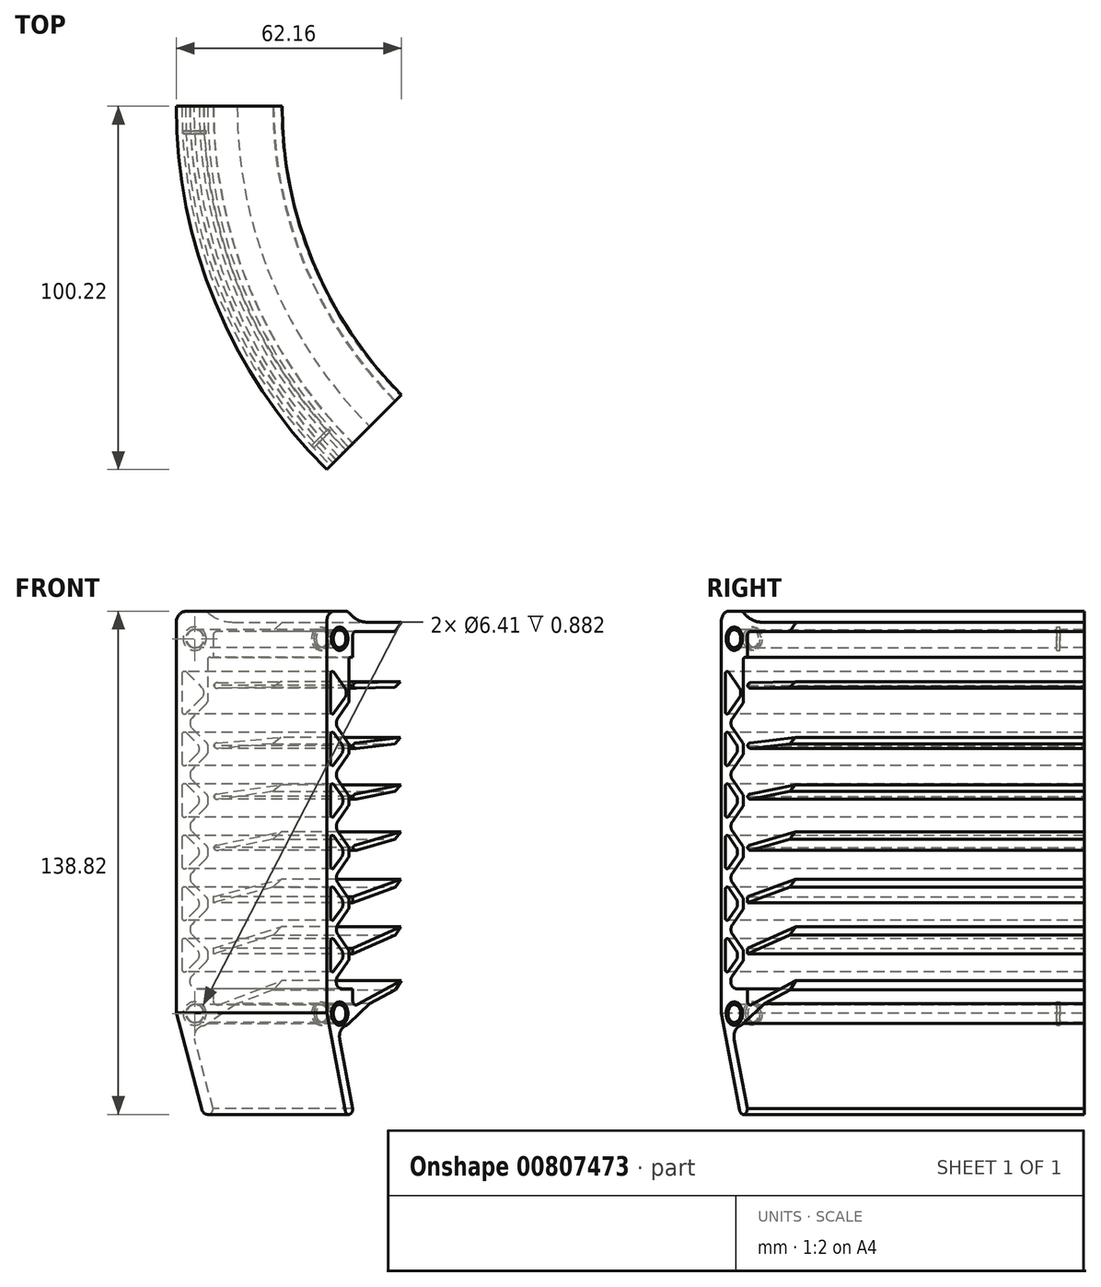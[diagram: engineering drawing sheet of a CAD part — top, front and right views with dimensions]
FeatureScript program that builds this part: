
annotation { "Feature Type Name" : "Feature", "Feature Type Description" : "" }
export const myFeature = defineFeature(function(context is Context, id is Id, definition is map)
    precondition{}
    {
        {
            var Q0;
            Q0=qCreatedBy(makeId("Front.planeOp"),FACE);
            var sketch = newSketch(context, id + "F0", { "sketchPlane" : qUnion([Q0])});
            skLineSegment(sketch, "E0", {"start": v(0, 0) * mm, "end": v(-133.7, 0) * mm, "construction": true});
            skLineSegment(sketch, "E1", {"start": v(-141.73, 0) * mm, "end": v(-141.73, 111.25) * mm});
            skLineSegment(sketch, "E2", {"start": v(-138.68, 114.3) * mm, "end": v(-134.62, 114.3) * mm});
            skLineSegment(sketch, "E3", {"start": v(-131.57, 111.25) * mm, "end": v(-131.57, 0) * mm});
            skLineSegment(sketch, "E4", {"start": v(-135.3, 101.6) * mm, "end": v(-131.57, 101.6) * mm});
            skLineSegment(sketch, "E5", {"start": v(-135.99, 10.16) * mm, "end": v(-131.57, 10.16) * mm});
            skLineSegment(sketch, "E6", {"start": v(-141.73, 3.56) * mm, "end": v(-134.54, -23.4) * mm});
            skLineSegment(sketch, "E7", {"start": v(-131.57, -23) * mm, "end": v(-131.57, -22.86) * mm});
            skLineSegment(sketch, "E8", {"start": v(-131.57, -22.86) * mm, "end": v(-136.65, -3.83) * mm});
            skPoint(sketch, "E9.visualSharp", {"position": v(-131.57, -34.54) * mm});
            skArc(sketch, "E9.filletArc", {"start": v(-134.54, -23.4) * mm, "mid": v(-132.89, -24.5) * mm, "end": v(-131.57, -23) * mm});
            skPoint(sketch, "E10.newPointA", {"position": v(-136.65, -3.8) * mm});
            skPoint(sketch, "E10.newPointB", {"position": v(-141.73, 0) * mm});
            skArc(sketch, "E10.filletArc", {"start": v(-133.7, 0) * mm, "mid": v(-136.12, -1.2) * mm, "end": v(-136.65, -3.83) * mm});
            skPoint(sketch, "E11.visualSharp", {"position": v(-141.73, 114.3) * mm});
            skArc(sketch, "E11.filletArc", {"start": v(-138.68, 114.3) * mm, "mid": v(-140.84, 113.4) * mm, "end": v(-141.73, 111.25) * mm});
            skPoint(sketch, "E12.visualSharp", {"position": v(-131.57, 114.3) * mm});
            skArc(sketch, "E12.filletArc", {"start": v(-131.57, 111.25) * mm, "mid": v(-132.46, 113.4) * mm, "end": v(-134.62, 114.3) * mm});
            skLineSegment(sketch, "E13.bottom", {"start": v(-140.2, 101.6) * mm, "end": v(-133.1, 101.6) * mm});
            skLineSegment(sketch, "E13.top", {"start": v(-140.2, 10.16) * mm, "end": v(-133.1, 10.16) * mm});
            skLineSegment(sketch, "E13.left", {"start": v(-140.2, 101.6) * mm, "end": v(-140.2, 10.16) * mm});
            skLineSegment(sketch, "E13.right", {"start": v(-133.1, 101.6) * mm, "end": v(-133.1, 10.16) * mm});
            skLineSegment(sketch, "E14", {"start": v(-136.74, 98.13) * mm, "end": v(-133.1, 94.49) * mm});
            skLineSegment(sketch, "E15", {"start": v(-134.7, 90.35) * mm, "end": v(-140.2, 84.84) * mm});
            skLineSegment(sketch, "E16", {"start": v(-137.34, 81.96) * mm, "end": v(-133.1, 77.72) * mm});
            skLineSegment(sketch, "E17", {"start": v(-135.97, 74.85) * mm, "end": v(-140.2, 70.61) * mm});
            skLineSegment(sketch, "E18", {"start": v(-137.34, 67.74) * mm, "end": v(-133.1, 63.5) * mm});
            skLineSegment(sketch, "E19", {"start": v(-135.97, 60.63) * mm, "end": v(-140.2, 56.39) * mm});
            skLineSegment(sketch, "E20", {"start": v(-137.34, 53.52) * mm, "end": v(-133.1, 49.28) * mm});
            skLineSegment(sketch, "E21", {"start": v(-135.97, 46.4) * mm, "end": v(-140.2, 42.16) * mm});
            skLineSegment(sketch, "E22", {"start": v(-137.34, 39.3) * mm, "end": v(-133.1, 35.05) * mm});
            skLineSegment(sketch, "E23", {"start": v(-135.97, 32.18) * mm, "end": v(-140.2, 27.94) * mm});
            skLineSegment(sketch, "E24", {"start": v(-137.34, 25.07) * mm, "end": v(-133.1, 20.83) * mm});
            skLineSegment(sketch, "E25", {"start": v(-135.97, 17.96) * mm, "end": v(-140.2, 13.72) * mm});
            skLineSegment(sketch, "E26.1.0.0", {"start": v(-133.1, 32.18) * mm, "end": v(-137.34, 27.94) * mm});
            skLineSegment(sketch, "E26.1.0.1", {"start": v(-140.2, 39.3) * mm, "end": v(-135.97, 35.05) * mm});
            skLineSegment(sketch, "E26.1.0.2", {"start": v(-140.2, 25.07) * mm, "end": v(-135.97, 20.83) * mm});
            skLineSegment(sketch, "E26.1.0.3", {"start": v(-133.1, 17.96) * mm, "end": v(-137.42, 13.63) * mm});
            skLineSegment(sketch, "E26.1.0.4", {"start": v(-133.1, 46.4) * mm, "end": v(-137.34, 42.17) * mm});
            skLineSegment(sketch, "E26.1.0.5", {"start": v(-140.2, 53.52) * mm, "end": v(-135.97, 49.28) * mm});
            skLineSegment(sketch, "E26.1.0.6", {"start": v(-133.1, 60.63) * mm, "end": v(-137.34, 56.39) * mm});
            skLineSegment(sketch, "E26.1.0.7", {"start": v(-140.2, 67.74) * mm, "end": v(-135.97, 63.5) * mm});
            skLineSegment(sketch, "E26.1.0.8", {"start": v(-133.1, 74.85) * mm, "end": v(-137.34, 70.61) * mm});
            skLineSegment(sketch, "E26.1.0.9", {"start": v(-140.2, 81.97) * mm, "end": v(-135.97, 77.73) * mm});
            skLineSegment(sketch, "E26.1.0.10", {"start": v(-133.1, 89.08) * mm, "end": v(-137.34, 84.84) * mm});
            skLineSegment(sketch, "E26.1.0.11", {"start": v(-140.2, 98.73) * mm, "end": v(-134.7, 93.22) * mm});
            skLineSegment(sketch, "E26.direction1", {"start": v(-140.2, 13.72) * mm, "end": v(-140.2, 11.43) * mm, "construction": true});
            skPoint(sketch, "E27.newPointA", {"position": v(-140.2, 101.6) * mm});
            skArc(sketch, "E27.filletArc", {"start": v(-135.3, 101.6) * mm, "mid": v(-137.18, 100.35) * mm, "end": v(-136.74, 98.13) * mm});
            skPoint(sketch, "E28.newPointA", {"position": v(-140.2, 10.85) * mm});
            skArc(sketch, "E28.filletArc", {"start": v(-137.42, 13.63) * mm, "mid": v(-137.87, 11.41) * mm, "end": v(-135.99, 10.16) * mm});
            skPoint(sketch, "E29.newPointA", {"position": v(-133.1, 17.96) * mm});
            skPoint(sketch, "E29.newPointB", {"position": v(-133.1, 20.83) * mm});
            skArc(sketch, "E29.filletArc", {"start": v(-135.97, 17.96) * mm, "mid": v(-135.37, 19.4) * mm, "end": v(-135.97, 20.83) * mm});
            skPoint(sketch, "E30.newPointA", {"position": v(-140.2, 27.94) * mm});
            skPoint(sketch, "E30.newPointB", {"position": v(-140.2, 25.07) * mm});
            skArc(sketch, "E30.filletArc", {"start": v(-137.34, 27.94) * mm, "mid": v(-137.93, 26.5) * mm, "end": v(-137.34, 25.07) * mm});
            skPoint(sketch, "E31.newPointA", {"position": v(-140.2, 42.16) * mm});
            skPoint(sketch, "E31.newPointB", {"position": v(-140.2, 39.3) * mm});
            skArc(sketch, "E31.filletArc", {"start": v(-137.34, 42.17) * mm, "mid": v(-137.93, 40.73) * mm, "end": v(-137.34, 39.3) * mm});
            skPoint(sketch, "E32.newPointA", {"position": v(-133.1, 49.28) * mm});
            skPoint(sketch, "E32.newPointB", {"position": v(-133.1, 46.4) * mm});
            skArc(sketch, "E32.filletArc", {"start": v(-135.97, 46.4) * mm, "mid": v(-135.37, 47.84) * mm, "end": v(-135.97, 49.28) * mm});
            skPoint(sketch, "E33.newPointA", {"position": v(-140.2, 56.39) * mm});
            skPoint(sketch, "E33.newPointB", {"position": v(-140.2, 53.52) * mm});
            skArc(sketch, "E33.filletArc", {"start": v(-137.34, 56.39) * mm, "mid": v(-137.93, 54.95) * mm, "end": v(-137.34, 53.52) * mm});
            skPoint(sketch, "E34.newPointA", {"position": v(-133.1, 63.5) * mm});
            skPoint(sketch, "E34.newPointB", {"position": v(-133.1, 60.63) * mm});
            skArc(sketch, "E34.filletArc", {"start": v(-135.97, 60.63) * mm, "mid": v(-135.37, 62.06) * mm, "end": v(-135.97, 63.5) * mm});
            skPoint(sketch, "E35.newPointA", {"position": v(-140.2, 70.61) * mm});
            skPoint(sketch, "E35.newPointB", {"position": v(-140.2, 67.74) * mm});
            skArc(sketch, "E35.filletArc", {"start": v(-137.34, 70.61) * mm, "mid": v(-137.93, 69.18) * mm, "end": v(-137.34, 67.74) * mm});
            skPoint(sketch, "E36.newPointA", {"position": v(-133.1, 35.05) * mm});
            skPoint(sketch, "E36.newPointB", {"position": v(-133.1, 32.18) * mm});
            skArc(sketch, "E36.filletArc", {"start": v(-135.97, 32.18) * mm, "mid": v(-135.37, 33.62) * mm, "end": v(-135.97, 35.05) * mm});
            skPoint(sketch, "E37.newPointA", {"position": v(-133.1, 77.72) * mm});
            skPoint(sketch, "E37.newPointB", {"position": v(-133.1, 74.85) * mm});
            skArc(sketch, "E37.filletArc", {"start": v(-135.97, 74.85) * mm, "mid": v(-135.37, 76.29) * mm, "end": v(-135.97, 77.73) * mm});
            skPoint(sketch, "E38.newPointA", {"position": v(-140.2, 84.84) * mm});
            skPoint(sketch, "E38.newPointB", {"position": v(-140.2, 81.97) * mm});
            skArc(sketch, "E38.filletArc", {"start": v(-137.34, 84.84) * mm, "mid": v(-137.93, 83.4) * mm, "end": v(-137.34, 81.96) * mm});
            skPoint(sketch, "E39.newPointA", {"position": v(-133.1, 91.95) * mm});
            skPoint(sketch, "E39.newPointB", {"position": v(-133.1, 91.62) * mm});
            skArc(sketch, "E39.filletArc", {"start": v(-134.7, 90.35) * mm, "mid": v(-134.1, 91.78) * mm, "end": v(-134.7, 93.22) * mm});
            skLineSegment(sketch, "E40", {"start": v(-136.65, -3.56) * mm, "end": v(-136.65, 10.16) * mm, "construction": true});
            skLineSegment(sketch, "E41", {"start": v(-136.65, 101.6) * mm, "end": v(-136.65, 106.68) * mm, "construction": true});
            skCircle(sketch, "E42", {"center": v(-136.65, 106.68) * mm, "radius": 2.48 * mm});
            skCircle(sketch, "E43", {"center": v(-136.65, 3.3) * mm, "radius": 2.48 * mm});
            skPoint(sketch, "E43.perimeterSnap0", {"position": v(-136.65, 3.3) * mm});
            skPoint(sketch, "E43.perimeterSnap1", {"position": v(-133.78, 10.16) * mm});
            skLineSegment(sketch, "E44", {"start": v(0, 0) * mm, "end": v(0, 14.7) * mm, "construction": true});
            skLineSegment(sketch, "E45", {"start": v(-111.76, 0) * mm, "end": v(-111.76, 130.03) * mm, "construction": true});
            skLineSegment(sketch, "E46", {"start": v(-131.57, 111.25) * mm, "end": v(-111.76, 111.25) * mm});
            skLineSegment(sketch, "E47", {"start": v(-111.76, 111.25) * mm, "end": v(-111.76, 108.71) * mm});
            skLineSegment(sketch, "E48", {"start": v(-111.76, 108.71) * mm, "end": v(-131.57, 108.71) * mm});
            skLineSegment(sketch, "E49", {"start": v(-111.76, 111.25) * mm, "end": v(111.76, 111.25) * mm, "construction": true});
            skLineSegment(sketch, "E50", {"start": v(111.76, 111.25) * mm, "end": v(111.76, 98.55) * mm, "construction": true});
            skLineSegment(sketch, "E51", {"start": v(-133.1, 94.49) * mm, "end": v(111.76, 98.55) * mm, "construction": true});
            skLineSegment(sketch, "E52", {"start": v(111.76, 98.55) * mm, "end": v(-133.1, 77.72) * mm, "construction": true});
            skLineSegment(sketch, "E53", {"start": v(111.76, 98.55) * mm, "end": v(-133.1, 63.5) * mm, "construction": true});
            skLineSegment(sketch, "E54", {"start": v(-133.1, 49.28) * mm, "end": v(111.76, 98.55) * mm, "construction": true});
            skLineSegment(sketch, "E55", {"start": v(-133.1, 35.05) * mm, "end": v(111.76, 98.55) * mm, "construction": true});
            skLineSegment(sketch, "E56", {"start": v(-133.1, 20.83) * mm, "end": v(111.76, 98.55) * mm, "construction": true});
            skLineSegment(sketch, "E57", {"start": v(-131.57, 10.16) * mm, "end": v(-131.57, 0) * mm, "construction": true});
            skLineSegment(sketch, "E58", {"start": v(-131.57, 5.08) * mm, "end": v(111.76, 98.55) * mm, "construction": true});
            skLineSegment(sketch, "E59", {"start": v(-131.57, 94.51) * mm, "end": v(-111.76, 94.84) * mm});
            skLineSegment(sketch, "E60", {"start": v(-111.76, 94.84) * mm, "end": v(-111.76, 93.32) * mm});
            skLineSegment(sketch, "E61", {"start": v(-111.76, 93.32) * mm, "end": v(-131.57, 92.99) * mm});
            skLineSegment(sketch, "E62", {"start": v(-131.57, 77.85) * mm, "end": v(-111.76, 79.54) * mm});
            skLineSegment(sketch, "E63", {"start": v(-111.76, 79.54) * mm, "end": v(-111.76, 78) * mm});
            skLineSegment(sketch, "E64", {"start": v(-111.76, 78) * mm, "end": v(-131.57, 76.32) * mm});
            skLineSegment(sketch, "E65", {"start": v(-131.57, 63.72) * mm, "end": v(-111.76, 66.55) * mm});
            skLineSegment(sketch, "E66", {"start": v(-111.76, 66.55) * mm, "end": v(-111.76, 65.01) * mm});
            skLineSegment(sketch, "E67", {"start": v(-111.76, 65.01) * mm, "end": v(-131.57, 62.18) * mm});
            skLineSegment(sketch, "E68", {"start": v(-131.57, 49.58) * mm, "end": v(-111.76, 53.57) * mm});
            skLineSegment(sketch, "E69", {"start": v(-111.76, 53.57) * mm, "end": v(-111.76, 52.02) * mm});
            skLineSegment(sketch, "E70", {"start": v(-111.76, 52.02) * mm, "end": v(-131.57, 48.03) * mm});
            skLineSegment(sketch, "E71", {"start": v(-131.57, 35.45) * mm, "end": v(-111.76, 40.59) * mm});
            skLineSegment(sketch, "E72", {"start": v(-111.76, 40.59) * mm, "end": v(-111.76, 39.01) * mm});
            skLineSegment(sketch, "E73", {"start": v(-111.76, 39.01) * mm, "end": v(-131.57, 33.87) * mm});
            skLineSegment(sketch, "E74", {"start": v(-131.57, 21.31) * mm, "end": v(-111.76, 27.6) * mm});
            skLineSegment(sketch, "E75", {"start": v(-111.76, 27.6) * mm, "end": v(-111.76, 26) * mm});
            skLineSegment(sketch, "E76", {"start": v(-111.76, 26) * mm, "end": v(-131.57, 19.71) * mm});
            skLineSegment(sketch, "E77", {"start": v(-131.57, 5.08) * mm, "end": v(-111.76, 12.7) * mm});
            skLineSegment(sketch, "E78", {"start": v(-111.76, 12.7) * mm, "end": v(-111.76, 11.06) * mm});
            skLineSegment(sketch, "E79", {"start": v(-111.76, 11.06) * mm, "end": v(-131.57, 3.45) * mm});
            skLineSegment(sketch, "E80", {"start": v(-133.7, 0) * mm, "end": v(-131.57, 0) * mm});
            skLineSegment(sketch, "E81", {"start": v(-111.76, 111.25) * mm, "end": v(-110.33, 111.25) * mm});
            skLineSegment(sketch, "E82", {"start": v(-110.33, 111.25) * mm, "end": v(-111.76, 108.71) * mm});
            skSolve(sketch);
        }
        {
            var Q0;
            {var subQ0=sQuery(id+"F0.wireOp",EDGE,"E6");Q0=makeQuery(id+"F0.imprint","IMPRINT",FACE,{"disambiguationData":[TD([[makeQuery(id+"F0.imprint","IMPRINT",EDGE,{"derivedFrom":subQ0}),1.0]])]});}
            var Q1;
            {var subQ22=sQuery(id+"F0.wireOp",EDGE,"E1");Q1=makeQuery(id+"F0.imprint","IMPRINT",FACE,{"disambiguationData":[TD([[makeQuery(id+"F0.imprint","IMPRINT",EDGE,{"derivedFrom":subQ22}),-1.0]])]});}
            var Q2;
            {var subQ8=sQuery(id+"F0.wireOp",EDGE,"E4");Q2=makeQuery(id+"F0.imprint","IMPRINT",FACE,{"disambiguationData":[TD([[makeQuery(id+"F0.imprint","IMPRINT",EDGE,{"derivedFrom":subQ8}),-1.0]])]});}
            var Q3;
            {var subQ14=sQuery(id+"F0.wireOp",EDGE,"E14");Q3=makeQuery(id+"F0.imprint","IMPRINT",FACE,{"disambiguationData":[TD([[makeQuery(id+"F0.imprint","IMPRINT",EDGE,{"derivedFrom":subQ14}),-1.0]])]});}
            var Q4;
            {var subQ0=sQuery(id+"F0.wireOp",EDGE,"E46");Q4=makeQuery(id+"F0.imprint","IMPRINT",FACE,{"disambiguationData":[TD([[makeQuery(id+"F0.imprint","IMPRINT",EDGE,{"derivedFrom":subQ0}),-1.0]])]});}
            var Q5;
            {var subQ0=sQuery(id+"F0.wireOp",EDGE,"E59");Q5=makeQuery(id+"F0.imprint","IMPRINT",FACE,{"disambiguationData":[TD([[makeQuery(id+"F0.imprint","IMPRINT",EDGE,{"derivedFrom":subQ0}),-1.0]])]});}
            var Q6;
            {var subQ0=sQuery(id+"F0.wireOp",EDGE,"E62");Q6=makeQuery(id+"F0.imprint","IMPRINT",FACE,{"disambiguationData":[TD([[makeQuery(id+"F0.imprint","IMPRINT",EDGE,{"derivedFrom":subQ0}),-1.0]])]});}
            var Q7;
            {var subQ0=sQuery(id+"F0.wireOp",EDGE,"E65");Q7=makeQuery(id+"F0.imprint","IMPRINT",FACE,{"disambiguationData":[TD([[makeQuery(id+"F0.imprint","IMPRINT",EDGE,{"derivedFrom":subQ0}),-1.0]])]});}
            var Q8;
            {var subQ0=sQuery(id+"F0.wireOp",EDGE,"E68");Q8=makeQuery(id+"F0.imprint","IMPRINT",FACE,{"disambiguationData":[TD([[makeQuery(id+"F0.imprint","IMPRINT",EDGE,{"derivedFrom":subQ0}),-1.0]])]});}
            var Q9;
            {var subQ0=sQuery(id+"F0.wireOp",EDGE,"E71");Q9=makeQuery(id+"F0.imprint","IMPRINT",FACE,{"disambiguationData":[TD([[makeQuery(id+"F0.imprint","IMPRINT",EDGE,{"derivedFrom":subQ0}),-1.0]])]});}
            var Q10;
            {var subQ0=sQuery(id+"F0.wireOp",EDGE,"E74");Q10=makeQuery(id+"F0.imprint","IMPRINT",FACE,{"disambiguationData":[TD([[makeQuery(id+"F0.imprint","IMPRINT",EDGE,{"derivedFrom":subQ0}),-1.0]])]});}
            var Q11;
            {var subQ0=sQuery(id+"F0.wireOp",EDGE,"E77");Q11=makeQuery(id+"F0.imprint","IMPRINT",FACE,{"disambiguationData":[TD([[makeQuery(id+"F0.imprint","IMPRINT",EDGE,{"derivedFrom":subQ0}),-1.0]])]});}
            var Q12;
            Q12=sQuery(id+"F0.wireOp",EDGE,"E44");
            revolve(context, id + "F1", {"surfaceOperationType" : NewSurfaceOperationType.NEW, "entities" : qUnion([Q0, Q1, Q2, Q3, Q4, Q5, Q6, Q7, Q8, Q9, Q10, Q11]), "axis" : qUnion([Q12]), "revolveType" : RevolveType.ONE_DIRECTION, "angle" : 45 * degree});
        }
        {
            var Q0;
            Q0=makeQuery(id+"F1.opRevolve","SWEPT_EDGE",EDGE,{"disambiguationData":[OSD([sQuery(id+"F0.wireOp",EDGE,"E47"),sQuery(id+"F0.wireOp",EDGE,"E48")])]});
            chamfer(context, id + "F2", {"entities" : qUnion([Q0]), "width" : 3.3 * mm, "tangentPropagation" : true});
        }
        {
            var Q0;
            Q0=makeQuery(id+"F1.opRevolve","SWEPT_EDGE",EDGE,{"disambiguationData":[OSD([sQuery(id+"F0.wireOp",EDGE,"E60"),sQuery(id+"F0.wireOp",EDGE,"E61")])]});
            var Q1;
            Q1=makeQuery(id+"F1.opRevolve","SWEPT_EDGE",EDGE,{"disambiguationData":[OSD([sQuery(id+"F0.wireOp",EDGE,"E63"),sQuery(id+"F0.wireOp",EDGE,"E64")])]});
            var Q2;
            Q2=makeQuery(id+"F1.opRevolve","SWEPT_EDGE",EDGE,{"disambiguationData":[OSD([sQuery(id+"F0.wireOp",EDGE,"E66"),sQuery(id+"F0.wireOp",EDGE,"E67")])]});
            var Q3;
            Q3=makeQuery(id+"F1.opRevolve","SWEPT_EDGE",EDGE,{"disambiguationData":[OSD([sQuery(id+"F0.wireOp",EDGE,"E69"),sQuery(id+"F0.wireOp",EDGE,"E70")])]});
            var Q4;
            Q4=makeQuery(id+"F1.opRevolve","SWEPT_EDGE",EDGE,{"disambiguationData":[OSD([sQuery(id+"F0.wireOp",EDGE,"E72"),sQuery(id+"F0.wireOp",EDGE,"E73")])]});
            var Q5;
            Q5=makeQuery(id+"F1.opRevolve","SWEPT_EDGE",EDGE,{"disambiguationData":[OSD([sQuery(id+"F0.wireOp",EDGE,"E75"),sQuery(id+"F0.wireOp",EDGE,"E76")])]});
            var Q6;
            Q6=makeQuery(id+"F1.opRevolve","SWEPT_EDGE",EDGE,{"disambiguationData":[OSD([sQuery(id+"F0.wireOp",EDGE,"E78"),sQuery(id+"F0.wireOp",EDGE,"E79")])]});
            chamfer(context, id + "F3", {"entities" : qUnion([Q0, Q1, Q2, Q3, Q4, Q5, Q6]), "chamferType" : ChamferType.TWO_OFFSETS, "width1" : 2.3 * mm, "oppositeDirection" : false, "width2" : 3.3 * mm, "tangentPropagation" : true});
        }
        {
            var Q0;
            Q0=makeQuery(id+"F1.opRevolve","CAP_FACE",FACE,{"disambiguationData":[OSD([sQuery(id+"F0.wireOp",EDGE,"E1"),sQuery(id+"F0.wireOp",EDGE,"E2"),sQuery(id+"F0.wireOp",EDGE,"E3"),sQuery(id+"F0.wireOp",EDGE,"E6"),sQuery(id+"F0.wireOp",EDGE,"E7"),sQuery(id+"F0.wireOp",EDGE,"E8"),sQuery(id+"F0.wireOp",EDGE,"E9.filletArc"),sQuery(id+"F0.wireOp",EDGE,"E10.filletArc"),sQuery(id+"F0.wireOp",EDGE,"E11.filletArc"),sQuery(id+"F0.wireOp",EDGE,"E12.filletArc"),sQuery(id+"F0.wireOp",EDGE,"E13.bottom"),sQuery(id+"F0.wireOp",EDGE,"E13.top"),sQuery(id+"F0.wireOp",EDGE,"E13.left"),sQuery(id+"F0.wireOp",EDGE,"E13.right"),sQuery(id+"F0.wireOp",EDGE,"E14"),sQuery(id+"F0.wireOp",EDGE,"E15"),sQuery(id+"F0.wireOp",EDGE,"E16"),sQuery(id+"F0.wireOp",EDGE,"E17"),sQuery(id+"F0.wireOp",EDGE,"E18"),sQuery(id+"F0.wireOp",EDGE,"E19"),sQuery(id+"F0.wireOp",EDGE,"E20"),sQuery(id+"F0.wireOp",EDGE,"E21"),sQuery(id+"F0.wireOp",EDGE,"E22"),sQuery(id+"F0.wireOp",EDGE,"E23"),sQuery(id+"F0.wireOp",EDGE,"E24"),sQuery(id+"F0.wireOp",EDGE,"E25"),sQuery(id+"F0.wireOp",EDGE,"E26.1.0.0"),sQuery(id+"F0.wireOp",EDGE,"E26.1.0.1"),sQuery(id+"F0.wireOp",EDGE,"E26.1.0.2"),sQuery(id+"F0.wireOp",EDGE,"E26.1.0.3"),sQuery(id+"F0.wireOp",EDGE,"E26.1.0.4"),sQuery(id+"F0.wireOp",EDGE,"E26.1.0.5"),sQuery(id+"F0.wireOp",EDGE,"E26.1.0.6"),sQuery(id+"F0.wireOp",EDGE,"E26.1.0.7"),sQuery(id+"F0.wireOp",EDGE,"E26.1.0.8"),sQuery(id+"F0.wireOp",EDGE,"E26.1.0.9"),sQuery(id+"F0.wireOp",EDGE,"E26.1.0.10"),sQuery(id+"F0.wireOp",EDGE,"E26.1.0.11"),sQuery(id+"F0.wireOp",EDGE,"E27.filletArc"),sQuery(id+"F0.wireOp",EDGE,"E28.filletArc"),sQuery(id+"F0.wireOp",EDGE,"E29.filletArc"),sQuery(id+"F0.wireOp",EDGE,"E30.filletArc"),sQuery(id+"F0.wireOp",EDGE,"E31.filletArc"),sQuery(id+"F0.wireOp",EDGE,"E32.filletArc"),sQuery(id+"F0.wireOp",EDGE,"E33.filletArc"),sQuery(id+"F0.wireOp",EDGE,"E34.filletArc"),sQuery(id+"F0.wireOp",EDGE,"E35.filletArc"),sQuery(id+"F0.wireOp",EDGE,"E36.filletArc"),sQuery(id+"F0.wireOp",EDGE,"E37.filletArc"),sQuery(id+"F0.wireOp",EDGE,"E38.filletArc"),sQuery(id+"F0.wireOp",EDGE,"E39.filletArc"),sQuery(id+"F0.wireOp",EDGE,"E42"),sQuery(id+"F0.wireOp",EDGE,"E43"),sQuery(id+"F0.wireOp",EDGE,"E46"),sQuery(id+"F0.wireOp",EDGE,"E47"),sQuery(id+"F0.wireOp",EDGE,"E48"),sQuery(id+"F0.wireOp",EDGE,"E59"),sQuery(id+"F0.wireOp",EDGE,"E60"),sQuery(id+"F0.wireOp",EDGE,"E61"),sQuery(id+"F0.wireOp",EDGE,"E62"),sQuery(id+"F0.wireOp",EDGE,"E63"),sQuery(id+"F0.wireOp",EDGE,"E64"),sQuery(id+"F0.wireOp",EDGE,"E65"),sQuery(id+"F0.wireOp",EDGE,"E66"),sQuery(id+"F0.wireOp",EDGE,"E67"),sQuery(id+"F0.wireOp",EDGE,"E68"),sQuery(id+"F0.wireOp",EDGE,"E69"),sQuery(id+"F0.wireOp",EDGE,"E70"),sQuery(id+"F0.wireOp",EDGE,"E71"),sQuery(id+"F0.wireOp",EDGE,"E72"),sQuery(id+"F0.wireOp",EDGE,"E73"),sQuery(id+"F0.wireOp",EDGE,"E74"),sQuery(id+"F0.wireOp",EDGE,"E75"),sQuery(id+"F0.wireOp",EDGE,"E76"),sQuery(id+"F0.wireOp",EDGE,"E77"),sQuery(id+"F0.wireOp",EDGE,"E78"),sQuery(id+"F0.wireOp",EDGE,"E79"),sQuery(id+"F0.wireOp",EDGE,"E80")])],"isStart":false});
            var sketch = newSketch(context, id + "F4", { "sketchPlane" : qUnion([Q0])});
            skCircle(sketch, "E83.0", {"center": v(-136.65, 106.68) * mm, "radius": 2.48 * mm});
            skCircle(sketch, "E84.0", {"center": v(-136.65, 3.3) * mm, "radius": 2.48 * mm});
            skCircle(sketch, "E85", {"center": v(-136.65, 106.68) * mm, "radius": 3.2 * mm});
            skCircle(sketch, "E86", {"center": v(-136.65, 3.3) * mm, "radius": 3.2 * mm});
            skSolve(sketch);
        }
        {
            var Q0;
            Q0=makeQuery(id+"F1.opRevolve","CAP_FACE",FACE,{"disambiguationData":[OSD([sQuery(id+"F0.wireOp",EDGE,"E1"),sQuery(id+"F0.wireOp",EDGE,"E2"),sQuery(id+"F0.wireOp",EDGE,"E3"),sQuery(id+"F0.wireOp",EDGE,"E6"),sQuery(id+"F0.wireOp",EDGE,"E7"),sQuery(id+"F0.wireOp",EDGE,"E8"),sQuery(id+"F0.wireOp",EDGE,"E9.filletArc"),sQuery(id+"F0.wireOp",EDGE,"E10.filletArc"),sQuery(id+"F0.wireOp",EDGE,"E11.filletArc"),sQuery(id+"F0.wireOp",EDGE,"E12.filletArc"),sQuery(id+"F0.wireOp",EDGE,"E13.bottom"),sQuery(id+"F0.wireOp",EDGE,"E13.top"),sQuery(id+"F0.wireOp",EDGE,"E13.left"),sQuery(id+"F0.wireOp",EDGE,"E13.right"),sQuery(id+"F0.wireOp",EDGE,"E14"),sQuery(id+"F0.wireOp",EDGE,"E15"),sQuery(id+"F0.wireOp",EDGE,"E16"),sQuery(id+"F0.wireOp",EDGE,"E17"),sQuery(id+"F0.wireOp",EDGE,"E18"),sQuery(id+"F0.wireOp",EDGE,"E19"),sQuery(id+"F0.wireOp",EDGE,"E20"),sQuery(id+"F0.wireOp",EDGE,"E21"),sQuery(id+"F0.wireOp",EDGE,"E22"),sQuery(id+"F0.wireOp",EDGE,"E23"),sQuery(id+"F0.wireOp",EDGE,"E24"),sQuery(id+"F0.wireOp",EDGE,"E25"),sQuery(id+"F0.wireOp",EDGE,"E26.1.0.0"),sQuery(id+"F0.wireOp",EDGE,"E26.1.0.1"),sQuery(id+"F0.wireOp",EDGE,"E26.1.0.2"),sQuery(id+"F0.wireOp",EDGE,"E26.1.0.3"),sQuery(id+"F0.wireOp",EDGE,"E26.1.0.4"),sQuery(id+"F0.wireOp",EDGE,"E26.1.0.5"),sQuery(id+"F0.wireOp",EDGE,"E26.1.0.6"),sQuery(id+"F0.wireOp",EDGE,"E26.1.0.7"),sQuery(id+"F0.wireOp",EDGE,"E26.1.0.8"),sQuery(id+"F0.wireOp",EDGE,"E26.1.0.9"),sQuery(id+"F0.wireOp",EDGE,"E26.1.0.10"),sQuery(id+"F0.wireOp",EDGE,"E26.1.0.11"),sQuery(id+"F0.wireOp",EDGE,"E27.filletArc"),sQuery(id+"F0.wireOp",EDGE,"E28.filletArc"),sQuery(id+"F0.wireOp",EDGE,"E29.filletArc"),sQuery(id+"F0.wireOp",EDGE,"E30.filletArc"),sQuery(id+"F0.wireOp",EDGE,"E31.filletArc"),sQuery(id+"F0.wireOp",EDGE,"E32.filletArc"),sQuery(id+"F0.wireOp",EDGE,"E33.filletArc"),sQuery(id+"F0.wireOp",EDGE,"E34.filletArc"),sQuery(id+"F0.wireOp",EDGE,"E35.filletArc"),sQuery(id+"F0.wireOp",EDGE,"E36.filletArc"),sQuery(id+"F0.wireOp",EDGE,"E37.filletArc"),sQuery(id+"F0.wireOp",EDGE,"E38.filletArc"),sQuery(id+"F0.wireOp",EDGE,"E39.filletArc"),sQuery(id+"F0.wireOp",EDGE,"E42"),sQuery(id+"F0.wireOp",EDGE,"E43"),sQuery(id+"F0.wireOp",EDGE,"E46"),sQuery(id+"F0.wireOp",EDGE,"E47"),sQuery(id+"F0.wireOp",EDGE,"E48"),sQuery(id+"F0.wireOp",EDGE,"E59"),sQuery(id+"F0.wireOp",EDGE,"E60"),sQuery(id+"F0.wireOp",EDGE,"E61"),sQuery(id+"F0.wireOp",EDGE,"E62"),sQuery(id+"F0.wireOp",EDGE,"E63"),sQuery(id+"F0.wireOp",EDGE,"E64"),sQuery(id+"F0.wireOp",EDGE,"E65"),sQuery(id+"F0.wireOp",EDGE,"E66"),sQuery(id+"F0.wireOp",EDGE,"E67"),sQuery(id+"F0.wireOp",EDGE,"E68"),sQuery(id+"F0.wireOp",EDGE,"E69"),sQuery(id+"F0.wireOp",EDGE,"E70"),sQuery(id+"F0.wireOp",EDGE,"E71"),sQuery(id+"F0.wireOp",EDGE,"E72"),sQuery(id+"F0.wireOp",EDGE,"E73"),sQuery(id+"F0.wireOp",EDGE,"E74"),sQuery(id+"F0.wireOp",EDGE,"E75"),sQuery(id+"F0.wireOp",EDGE,"E76"),sQuery(id+"F0.wireOp",EDGE,"E77"),sQuery(id+"F0.wireOp",EDGE,"E78"),sQuery(id+"F0.wireOp",EDGE,"E79"),sQuery(id+"F0.wireOp",EDGE,"E80")])],"isStart":true});
            var sketch = newSketch(context, id + "F5", { "sketchPlane" : qUnion([Q0])});
            skCircle(sketch, "E87", {"center": v(136.65, 106.68) * mm, "radius": 3.2 * mm});
            skCircle(sketch, "E88", {"center": v(136.65, 3.3) * mm, "radius": 3.2 * mm});
            skSolve(sketch);
        }
        {
            var Q0;
            Q0=makeQuery(id+"F5.imprint","IMPRINT",FACE,{"disambiguationData":[TD([[makeQuery(id+"F5.imprint","IMPRINT",EDGE,{"derivedFrom":sQuery(id+"F5.wireOp",EDGE,"E87")}),1.0]])]});
            var Q1;
            Q1=makeQuery(id+"F5.imprint","IMPRINT",FACE,{"disambiguationData":[TD([[makeQuery(id+"F5.imprint","IMPRINT",EDGE,{"derivedFrom":sQuery(id+"F5.wireOp",EDGE,"E88")}),1.0]])]});
            var Q2;
            Q2 = qSketchRegion(id + "F10", true);
            extrude(context, id + "F6", {"entities" : qUnion([Q0, Q1, Q2]), "operationType" : NewBodyOperationType.REMOVE, "oppositeDirection" : true, "depth" : ((.3008 - .2314) / 2) * mm, "offsetDistance" : 25.4 * mm});
        }
        {
            var Q0;
            Q0=makeQuery(id+"F4.imprint","IMPRINT",FACE,{"disambiguationData":[TD([[makeQuery(id+"F4.imprint","IMPRINT",EDGE,{"derivedFrom":sQuery(id+"F4.wireOp",EDGE,"E83.0")}),-1.0]])]});
            var Q1;
            Q1=makeQuery(id+"F4.imprint","IMPRINT",FACE,{"disambiguationData":[TD([[makeQuery(id+"F4.imprint","IMPRINT",EDGE,{"derivedFrom":sQuery(id+"F4.wireOp",EDGE,"E84.0")}),-1.0]])]});
            extrude(context, id + "F7", {"entities" : qUnion([Q0, Q1]), "operationType" : NewBodyOperationType.REMOVE, "oppositeDirection" : true, "depth" : ((.3008 - .2314) / 2) * mm, "offsetDistance" : 25.4 * mm});
        }
        {
            var Q0;
            Q0=makeQuery(id+"F1.opRevolve","SWEPT_FACE",FACE,{"disambiguationData":[OSD([sQuery(id+"F0.wireOp",EDGE,"E2")])]});
            var sketch = newSketch(context, id + "F8", { "sketchPlane" : qUnion([Q0])});
            skPoint(sketch, "E89.0", {"position": v(-136.65, 0) * mm});
            skPoint(sketch, "E90.0", {"position": v(-134.62, 0) * mm});
            skLineSegment(sketch, "E91.0", {"start": v(-138.68, 0) * mm, "end": v(-134.62, 0) * mm});
            skLineSegment(sketch, "E92.0", {"start": v(-98.06, -98.06) * mm, "end": v(-95.2, -95.2) * mm});
            skLineSegment(sketch, "E93", {"start": v(-136.65, 0) * mm, "end": v(-136.65, -6.76) * mm, "construction": true});
            skLineSegment(sketch, "E94", {"start": v(-96.63, -96.63) * mm, "end": v(-101.4, -91.85) * mm, "construction": true});
            skLineSegment(sketch, "E95", {"start": v(-101.4, -91.85) * mm, "end": v(-96.76, -87.2) * mm});
            skLineSegment(sketch, "E96", {"start": v(-101.4, -91.85) * mm, "end": v(-106.73, -97.17) * mm});
            skLineSegment(sketch, "E97", {"start": v(-136.65, -6.76) * mm, "end": v(-131.83, -6.76) * mm});
            skLineSegment(sketch, "E98", {"start": v(-136.65, -6.76) * mm, "end": v(-140.36, -6.76) * mm});
            skLineSegment(sketch, "E99", {"start": v(-136.65, -6.76) * mm, "end": v(-136.65, -7.64) * mm});
            skLineSegment(sketch, "E100", {"start": v(-101.4, -91.85) * mm, "end": v(-102.03, -91.23) * mm});
            skLineSegment(sketch, "E101", {"start": v(-102.03, -91.23) * mm, "end": v(-97.96, -87.15) * mm});
            skLineSegment(sketch, "E102", {"start": v(-102.03, -91.23) * mm, "end": v(-106.87, -96.07) * mm});
            skLineSegment(sketch, "E103", {"start": v(-136.65, -7.64) * mm, "end": v(-132.27, -7.64) * mm});
            skLineSegment(sketch, "E104", {"start": v(-136.65, -7.64) * mm, "end": v(-141.1, -7.64) * mm});
            skSolve(sketch);
        }
        {
            var Q0;
            Q0=sQuery(id+"F8.wireOp",EDGE,"E104");
            var Q1;
            Q1=sQuery(id+"F8.wireOp",EDGE,"E98");
            var Q2;
            Q2=sQuery(id+"F8.wireOp",EDGE,"E97");
            var Q3;
            Q3=sQuery(id+"F8.wireOp",EDGE,"E103");
            var Q4;
            Q4=sQuery(id+"F8.wireOp",EDGE,"E95");
            var Q5;
            Q5=sQuery(id+"F8.wireOp",EDGE,"E101");
            var Q6;
            Q6=sQuery(id+"F8.wireOp",EDGE,"E102");
            var Q7;
            Q7=sQuery(id+"F8.wireOp",EDGE,"E96");
            extrude(context, id + "F9", {"bodyType" : ToolBodyType.SURFACE, "surfaceEntities" : qUnion([Q0, Q1, Q2, Q3, Q4, Q5, Q6, Q7]), "oppositeDirection" : true, "depth" : 127 * mm, "offsetDistance" : 25.4 * mm});
        }
        {
            var Q0;
            Q0=makeQuery(id+"F9.opExtrude","SWEPT_FACE",FACE,{"disambiguationData":[OSD([sQuery(id+"F8.wireOp",EDGE,"E95"),sQuery(id+"F8.wireOp",EDGE,"E96")])]});
            var sketch = newSketch(context, id + "F10", { "sketchPlane" : qUnion([Q0])});
            skCircle(sketch, "E105.0", {"center": v(136.65, 106.68) * mm, "radius": 3.2 * mm});
            skCircle(sketch, "E106.0", {"center": v(136.65, 3.3) * mm, "radius": 3.2 * mm});
            skSolve(sketch);
        }
        {
            var Q0;
            Q0=makeQuery(id+"F9.opExtrude","SWEPT_FACE",FACE,{"disambiguationData":[OSD([sQuery(id+"F8.wireOp",EDGE,"E97"),sQuery(id+"F8.wireOp",EDGE,"E98")])]});
            var sketch = newSketch(context, id + "F11", { "sketchPlane" : qUnion([Q0])});
            skCircle(sketch, "E107.0", {"center": v(-136.65, 106.68) * mm, "radius": 3.2 * mm});
            skCircle(sketch, "E108.0", {"center": v(-136.65, 3.3) * mm, "radius": 3.2 * mm});
            skSolve(sketch);
        }
        {
            var Q0;
            Q0=makeQuery(id+"F11.imprint","IMPRINT",FACE,{"disambiguationData":[TD([[makeQuery(id+"F11.imprint","IMPRINT",EDGE,{"derivedFrom":sQuery(id+"F11.wireOp",EDGE,"E108.0")}),1.0]])]});
            var Q1;
            Q1=makeQuery(id+"F11.imprint","IMPRINT",FACE,{"disambiguationData":[TD([[makeQuery(id+"F11.imprint","IMPRINT",EDGE,{"derivedFrom":sQuery(id+"F11.wireOp",EDGE,"E107.0")}),1.0]])]});
            extrude(context, id + "F12", {"entities" : qUnion([Q0, Q1]), "operationType" : NewBodyOperationType.REMOVE, "depth" : 0.88 * mm, "offsetDistance" : 25.4 * mm});
        }
        {
            var Q0;
            Q0=makeQuery(id+"F10.imprint","IMPRINT",FACE,{"disambiguationData":[TD([[makeQuery(id+"F10.imprint","IMPRINT",EDGE,{"derivedFrom":sQuery(id+"F10.wireOp",EDGE,"E105.0")}),1.0]])]});
            var Q1;
            Q1=makeQuery(id+"F10.imprint","IMPRINT",FACE,{"disambiguationData":[TD([[makeQuery(id+"F10.imprint","IMPRINT",EDGE,{"derivedFrom":sQuery(id+"F10.wireOp",EDGE,"E106.0")}),1.0]])]});
            extrude(context, id + "F13", {"entities" : qUnion([Q0, Q1]), "operationType" : NewBodyOperationType.REMOVE, "depth" : 0.88 * mm, "offsetDistance" : 25.4 * mm});
        }
        {
            var Q0;
            Q0=makeQuery(id+"F1.opRevolve","SWEPT_EDGE",EDGE,{"disambiguationData":[OSD([sQuery(id+"F0.wireOp",EDGE,"E3"),sQuery(id+"F0.wireOp",EDGE,"E80")])]});
            fillet(context, id + "F14", {"entities" : qUnion([Q0]), "radius" : 3.8 * mm, "tangentPropagation" : true, "allowEdgeOverflow" : false});
        }
        {
            var Q0;
            Q0=makeQuery(id+"F14.opFillet","BLEND_EDGE",EDGE,{"blendedFrom":[makeQuery(id+"F1.opRevolve","SWEPT_EDGE",EDGE,{"disambiguationData":[OSD([sQuery(id+"F0.wireOp",EDGE,"E3"),sQuery(id+"F0.wireOp",EDGE,"E80")])]}),makeQuery(id+"F1.opRevolve","SWEPT_FACE",FACE,{"disambiguationData":[OSD([sQuery(id+"F0.wireOp",EDGE,"E79")])]})],"blendedInto":[makeQuery(id+"F1.opRevolve","SWEPT_FACE",FACE,{"disambiguationData":[OSD([sQuery(id+"F0.wireOp",EDGE,"E79")])]})]});
            chamfer(context, id + "F15", {"entities" : qUnion([Q0]), "chamferType" : ChamferType.TWO_OFFSETS, "width1" : 22.86 * mm, "oppositeDirection" : false, "width2" : 24.13 * mm, "tangentPropagation" : true});
        }
        {
            var Q0;
            Q0=makeQuery(id+"F1.opRevolve","SWEPT_EDGE",EDGE,{"disambiguationData":[OSD([sQuery(id+"F0.wireOp",EDGE,"E3"),sQuery(id+"F0.wireOp",EDGE,"E77")])]});
            var Q1;
            Q1=makeQuery(id+"F1.opRevolve","SWEPT_EDGE",EDGE,{"disambiguationData":[OSD([sQuery(id+"F0.wireOp",EDGE,"E3"),sQuery(id+"F0.wireOp",EDGE,"E74")])]});
            var Q2;
            Q2=makeQuery(id+"F1.opRevolve","SWEPT_EDGE",EDGE,{"disambiguationData":[OSD([sQuery(id+"F0.wireOp",EDGE,"E3"),sQuery(id+"F0.wireOp",EDGE,"E71")])]});
            var Q3;
            Q3=makeQuery(id+"F1.opRevolve","SWEPT_EDGE",EDGE,{"disambiguationData":[OSD([sQuery(id+"F0.wireOp",EDGE,"E3"),sQuery(id+"F0.wireOp",EDGE,"E68")])]});
            var Q4;
            Q4=makeQuery(id+"F1.opRevolve","SWEPT_EDGE",EDGE,{"disambiguationData":[OSD([sQuery(id+"F0.wireOp",EDGE,"E3"),sQuery(id+"F0.wireOp",EDGE,"E65")])]});
            var Q5;
            Q5=makeQuery(id+"F1.opRevolve","SWEPT_EDGE",EDGE,{"disambiguationData":[OSD([sQuery(id+"F0.wireOp",EDGE,"E3"),sQuery(id+"F0.wireOp",EDGE,"E62")])]});
            var Q6;
            Q6=makeQuery(id+"F1.opRevolve","SWEPT_EDGE",EDGE,{"disambiguationData":[OSD([sQuery(id+"F0.wireOp",EDGE,"E3"),sQuery(id+"F0.wireOp",EDGE,"E59")])]});
            var Q7;
            Q7=makeQuery(id+"F1.opRevolve","SWEPT_EDGE",EDGE,{"disambiguationData":[OSD([sQuery(id+"F0.wireOp",EDGE,"E3"),sQuery(id+"F0.wireOp",EDGE,"E76")])]});
            var Q8;
            Q8=makeQuery(id+"F1.opRevolve","SWEPT_EDGE",EDGE,{"disambiguationData":[OSD([sQuery(id+"F0.wireOp",EDGE,"E3"),sQuery(id+"F0.wireOp",EDGE,"E73")])]});
            var Q9;
            Q9=makeQuery(id+"F1.opRevolve","SWEPT_EDGE",EDGE,{"disambiguationData":[OSD([sQuery(id+"F0.wireOp",EDGE,"E3"),sQuery(id+"F0.wireOp",EDGE,"E70")])]});
            var Q10;
            Q10=makeQuery(id+"F1.opRevolve","SWEPT_EDGE",EDGE,{"disambiguationData":[OSD([sQuery(id+"F0.wireOp",EDGE,"E3"),sQuery(id+"F0.wireOp",EDGE,"E67")])]});
            var Q11;
            Q11=makeQuery(id+"F1.opRevolve","SWEPT_EDGE",EDGE,{"disambiguationData":[OSD([sQuery(id+"F0.wireOp",EDGE,"E3"),sQuery(id+"F0.wireOp",EDGE,"E64")])]});
            var Q12;
            Q12=makeQuery(id+"F1.opRevolve","SWEPT_EDGE",EDGE,{"disambiguationData":[OSD([sQuery(id+"F0.wireOp",EDGE,"E3"),sQuery(id+"F0.wireOp",EDGE,"E61")])]});
            var Q13;
            Q13=makeQuery(id+"F1.opRevolve","SWEPT_EDGE",EDGE,{"disambiguationData":[OSD([sQuery(id+"F0.wireOp",EDGE,"E3"),sQuery(id+"F0.wireOp",EDGE,"E48")])]});
            fillet(context, id + "F16", {"entities" : qUnion([Q0, Q1, Q2, Q3, Q4, Q5, Q6, Q7, Q8, Q9, Q10, Q11, Q12, Q13]), "radius" : 1.27 * mm, "tangentPropagation" : true, "allowEdgeOverflow" : false});
        }
        {
            var Q0;
            Q0=makeQuery(id+"F1.opRevolve","SWEPT_EDGE",EDGE,{"disambiguationData":[OSD([sQuery(id+"F0.wireOp",EDGE,"E3"),sQuery(id+"F0.wireOp",EDGE,"E12.filletArc"),sQuery(id+"F0.wireOp",EDGE,"E46")])]});
            fillet(context, id + "F17", {"entities" : qUnion([Q0]), "radius" : 10.16 * mm, "tangentPropagation" : true, "allowEdgeOverflow" : false});
        }
        {
            var Q0;
            Q0=makeQuery(id+"F1.opRevolve","SWEPT_EDGE",EDGE,{"disambiguationData":[OSD([sQuery(id+"F0.wireOp",EDGE,"E13.right"),sQuery(id+"F0.wireOp",EDGE,"E14")])]});
            var Q1;
            Q1=makeQuery(id+"F1.opRevolve","SWEPT_EDGE",EDGE,{"disambiguationData":[OSD([sQuery(id+"F0.wireOp",EDGE,"E13.right"),sQuery(id+"F0.wireOp",EDGE,"E16")])]});
            var Q2;
            Q2=makeQuery(id+"F1.opRevolve","SWEPT_EDGE",EDGE,{"disambiguationData":[OSD([sQuery(id+"F0.wireOp",EDGE,"E13.right"),sQuery(id+"F0.wireOp",EDGE,"E18")])]});
            var Q3;
            Q3=makeQuery(id+"F1.opRevolve","SWEPT_EDGE",EDGE,{"disambiguationData":[OSD([sQuery(id+"F0.wireOp",EDGE,"E13.right"),sQuery(id+"F0.wireOp",EDGE,"E20")])]});
            var Q4;
            Q4=makeQuery(id+"F1.opRevolve","SWEPT_EDGE",EDGE,{"disambiguationData":[OSD([sQuery(id+"F0.wireOp",EDGE,"E13.right"),sQuery(id+"F0.wireOp",EDGE,"E22")])]});
            var Q5;
            Q5=makeQuery(id+"F1.opRevolve","SWEPT_EDGE",EDGE,{"disambiguationData":[OSD([sQuery(id+"F0.wireOp",EDGE,"E13.right"),sQuery(id+"F0.wireOp",EDGE,"E24")])]});
            var Q6;
            Q6=makeQuery(id+"F1.opRevolve","SWEPT_EDGE",EDGE,{"disambiguationData":[OSD([sQuery(id+"F0.wireOp",EDGE,"E13.left"),sQuery(id+"F0.wireOp",EDGE,"E15")])]});
            var Q7;
            Q7=makeQuery(id+"F1.opRevolve","SWEPT_EDGE",EDGE,{"disambiguationData":[OSD([sQuery(id+"F0.wireOp",EDGE,"E13.left"),sQuery(id+"F0.wireOp",EDGE,"E17")])]});
            var Q8;
            Q8=makeQuery(id+"F1.opRevolve","SWEPT_EDGE",EDGE,{"disambiguationData":[OSD([sQuery(id+"F0.wireOp",EDGE,"E13.left"),sQuery(id+"F0.wireOp",EDGE,"E19")])]});
            var Q9;
            Q9=makeQuery(id+"F1.opRevolve","SWEPT_EDGE",EDGE,{"disambiguationData":[OSD([sQuery(id+"F0.wireOp",EDGE,"E13.left"),sQuery(id+"F0.wireOp",EDGE,"E21")])]});
            var Q10;
            Q10=makeQuery(id+"F1.opRevolve","SWEPT_EDGE",EDGE,{"disambiguationData":[OSD([sQuery(id+"F0.wireOp",EDGE,"E13.left"),sQuery(id+"F0.wireOp",EDGE,"E23")])]});
            var Q11;
            Q11=makeQuery(id+"F1.opRevolve","SWEPT_EDGE",EDGE,{"disambiguationData":[OSD([sQuery(id+"F0.wireOp",EDGE,"E13.left"),sQuery(id+"F0.wireOp",EDGE,"E25")])]});
            var Q12;
            Q12=makeQuery(id+"F1.opRevolve","SWEPT_EDGE",EDGE,{"disambiguationData":[OSD([sQuery(id+"F0.wireOp",EDGE,"E13.left"),sQuery(id+"F0.wireOp",EDGE,"E26.1.0.11")])]});
            var Q13;
            Q13=makeQuery(id+"F1.opRevolve","SWEPT_EDGE",EDGE,{"disambiguationData":[OSD([sQuery(id+"F0.wireOp",EDGE,"E13.left"),sQuery(id+"F0.wireOp",EDGE,"E26.1.0.9")])]});
            var Q14;
            Q14=makeQuery(id+"F1.opRevolve","SWEPT_EDGE",EDGE,{"disambiguationData":[OSD([sQuery(id+"F0.wireOp",EDGE,"E13.left"),sQuery(id+"F0.wireOp",EDGE,"E26.1.0.7")])]});
            var Q15;
            Q15=makeQuery(id+"F1.opRevolve","SWEPT_EDGE",EDGE,{"disambiguationData":[OSD([sQuery(id+"F0.wireOp",EDGE,"E13.left"),sQuery(id+"F0.wireOp",EDGE,"E26.1.0.5")])]});
            var Q16;
            Q16=makeQuery(id+"F1.opRevolve","SWEPT_EDGE",EDGE,{"disambiguationData":[OSD([sQuery(id+"F0.wireOp",EDGE,"E13.left"),sQuery(id+"F0.wireOp",EDGE,"E26.1.0.1")])]});
            var Q17;
            Q17=makeQuery(id+"F1.opRevolve","SWEPT_EDGE",EDGE,{"disambiguationData":[OSD([sQuery(id+"F0.wireOp",EDGE,"E13.left"),sQuery(id+"F0.wireOp",EDGE,"E26.1.0.2")])]});
            var Q18;
            Q18=makeQuery(id+"F1.opRevolve","SWEPT_EDGE",EDGE,{"disambiguationData":[OSD([sQuery(id+"F0.wireOp",EDGE,"E13.right"),sQuery(id+"F0.wireOp",EDGE,"E26.1.0.10")])]});
            var Q19;
            Q19=makeQuery(id+"F1.opRevolve","SWEPT_EDGE",EDGE,{"disambiguationData":[OSD([sQuery(id+"F0.wireOp",EDGE,"E13.right"),sQuery(id+"F0.wireOp",EDGE,"E26.1.0.8")])]});
            var Q20;
            Q20=makeQuery(id+"F1.opRevolve","SWEPT_EDGE",EDGE,{"disambiguationData":[OSD([sQuery(id+"F0.wireOp",EDGE,"E13.right"),sQuery(id+"F0.wireOp",EDGE,"E26.1.0.6")])]});
            var Q21;
            Q21=makeQuery(id+"F1.opRevolve","SWEPT_EDGE",EDGE,{"disambiguationData":[OSD([sQuery(id+"F0.wireOp",EDGE,"E13.right"),sQuery(id+"F0.wireOp",EDGE,"E26.1.0.4")])]});
            var Q22;
            Q22=makeQuery(id+"F1.opRevolve","SWEPT_EDGE",EDGE,{"disambiguationData":[OSD([sQuery(id+"F0.wireOp",EDGE,"E13.right"),sQuery(id+"F0.wireOp",EDGE,"E26.1.0.0")])]});
            var Q23;
            Q23=makeQuery(id+"F1.opRevolve","SWEPT_EDGE",EDGE,{"disambiguationData":[OSD([sQuery(id+"F0.wireOp",EDGE,"E13.right"),sQuery(id+"F0.wireOp",EDGE,"E26.1.0.3")])]});
            var Q24;
            Q24=makeQuery(id+"F1.opRevolve","SWEPT_EDGE",EDGE,{"disambiguationData":[OSD([sQuery(id+"F0.wireOp",EDGE,"E4"),sQuery(id+"F0.wireOp",EDGE,"E13.bottom"),sQuery(id+"F0.wireOp",EDGE,"E13.right")])]});
            var Q25;
            Q25=makeQuery(id+"F1.opRevolve","SWEPT_EDGE",EDGE,{"disambiguationData":[OSD([sQuery(id+"F0.wireOp",EDGE,"E5"),sQuery(id+"F0.wireOp",EDGE,"E13.top"),sQuery(id+"F0.wireOp",EDGE,"E13.right")])]});
            fillet(context, id + "F18", {"entities" : qUnion([Q0, Q1, Q2, Q3, Q4, Q5, Q6, Q7, Q8, Q9, Q10, Q11, Q12, Q13, Q14, Q15, Q16, Q17, Q18, Q19, Q20, Q21, Q22, Q23, Q24, Q25]), "radius" : 0.76 * mm, "tangentPropagation" : true, "allowEdgeOverflow" : false});
        }
    });
